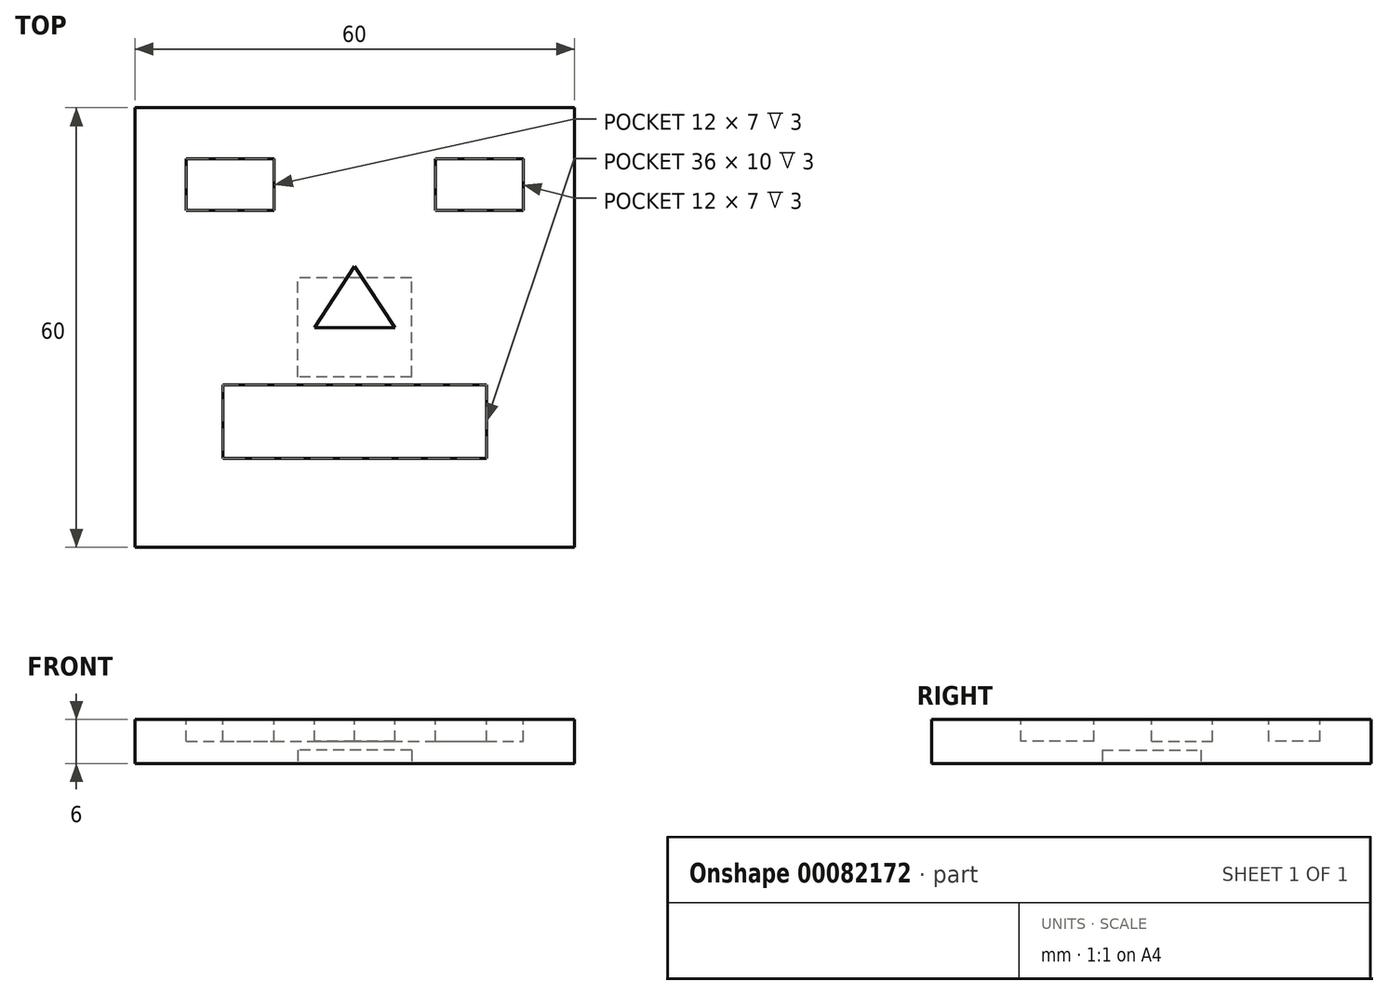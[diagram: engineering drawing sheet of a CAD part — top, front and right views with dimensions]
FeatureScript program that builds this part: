
annotation { "Feature Type Name" : "Feature", "Feature Type Description" : "" }
export const myFeature = defineFeature(function(context is Context, id is Id, definition is map)
    precondition{}
    {
        {
            var Q0;
            Q0=qCreatedBy(makeId("Top.planeOp"),FACE);
            var sketch = newSketch(context, id + "F0", { "sketchPlane" : qUnion([Q0])});
            skLineSegment(sketch, "E0.bottom", {"start": v(30, 30) * mm, "end": v(-30, 30) * mm});
            skLineSegment(sketch, "E0.top", {"start": v(30, -30) * mm, "end": v(-30, -30) * mm});
            skLineSegment(sketch, "E0.left", {"start": v(30, 30) * mm, "end": v(30, -30) * mm});
            skLineSegment(sketch, "E0.right", {"start": v(-30, 30) * mm, "end": v(-30, -30) * mm});
            skPoint(sketch, "E0.middle", {"position": v(0, 0) * mm});
            skSolve(sketch);
        }
        {
            var Q0;
            Q0 = qSketchRegion(id + "F0", true);
            extrude(context, id + "F1", {"entities" : qUnion([Q0]), "depth" : (6) * mm});
        }
        {
            var Q0;
            Q0=makeQuery(id+"F1.opExtrude","CAP_FACE",FACE,{"disambiguationData":[OSD([sQuery(id+"F0.wireOp",EDGE,"E0.bottom"),sQuery(id+"F0.wireOp",EDGE,"E0.top"),sQuery(id+"F0.wireOp",EDGE,"E0.left"),sQuery(id+"F0.wireOp",EDGE,"E0.right")])],"isStart":false});
            var sketch = newSketch(context, id + "F2", { "sketchPlane" : qUnion([Q0])});
            skLineSegment(sketch, "E1.bottom", {"start": v(-23, 23) * mm, "end": v(-11, 23) * mm});
            skLineSegment(sketch, "E1.top", {"start": v(-23, 16) * mm, "end": v(-11, 16) * mm});
            skLineSegment(sketch, "E1.left", {"start": v(-23, 23) * mm, "end": v(-23, 16) * mm});
            skLineSegment(sketch, "E1.right", {"start": v(-11, 23) * mm, "end": v(-11, 16) * mm});
            skLineSegment(sketch, "E2.bottom", {"start": v(11, 23) * mm, "end": v(23, 23) * mm});
            skLineSegment(sketch, "E2.top", {"start": v(11, 16) * mm, "end": v(23, 16) * mm});
            skLineSegment(sketch, "E2.left", {"start": v(11, 23) * mm, "end": v(11, 16) * mm});
            skLineSegment(sketch, "E2.right", {"start": v(23, 23) * mm, "end": v(23, 16) * mm});
            skLineSegment(sketch, "E3.bottom", {"start": v(-18, -7.84) * mm, "end": v(18, -7.84) * mm});
            skLineSegment(sketch, "E3.top", {"start": v(-18, -17.84) * mm, "end": v(18, -17.84) * mm});
            skLineSegment(sketch, "E3.left", {"start": v(-18, -7.84) * mm, "end": v(-18, -17.84) * mm});
            skLineSegment(sketch, "E3.right", {"start": v(18, -7.84) * mm, "end": v(18, -17.84) * mm});
            skLineSegment(sketch, "E4", {"start": v(0, 8.35) * mm, "end": v(-5.5, 0) * mm});
            skLineSegment(sketch, "E5", {"start": v(-5.5, 0) * mm, "end": v(5.5, 0) * mm});
            skLineSegment(sketch, "E6", {"start": v(5.5, 0) * mm, "end": v(0, 8.35) * mm});
            skSolve(sketch);
        }
        {
            var Q0;
            Q0 = qSketchRegion(id + "F2", true);
            extrude(context, id + "F3", {"entities" : qUnion([Q0]), "operationType" : NewBodyOperationType.REMOVE, "oppositeDirection" : true, "depth" : 3 * mm});
        }
        {
            var Q0;
            Q0=makeQuery(id+"F1.opExtrude","CAP_FACE",FACE,{"disambiguationData":[OSD([sQuery(id+"F0.wireOp",EDGE,"E0.bottom"),sQuery(id+"F0.wireOp",EDGE,"E0.top"),sQuery(id+"F0.wireOp",EDGE,"E0.left"),sQuery(id+"F0.wireOp",EDGE,"E0.right")])],"isStart":true});
            var sketch = newSketch(context, id + "F4", { "sketchPlane" : qUnion([Q0])});
            skLineSegment(sketch, "E7.bottom", {"start": v(7.75, 6.75) * mm, "end": v(-7.75, 6.75) * mm});
            skLineSegment(sketch, "E7.top", {"start": v(7.75, -6.75) * mm, "end": v(-7.75, -6.75) * mm});
            skLineSegment(sketch, "E7.left", {"start": v(7.75, 6.75) * mm, "end": v(7.75, -6.75) * mm});
            skLineSegment(sketch, "E7.right", {"start": v(-7.75, 6.75) * mm, "end": v(-7.75, -6.75) * mm});
            skPoint(sketch, "E7.middle", {"position": v(0, 0) * mm});
            skSolve(sketch);
        }
        {
            var Q0;
            Q0 = qSketchRegion(id + "F4", true);
            extrude(context, id + "F5", {"entities" : qUnion([Q0]), "operationType" : NewBodyOperationType.REMOVE, "oppositeDirection" : true, "depth" : 1.8 * mm});
        }
    });
